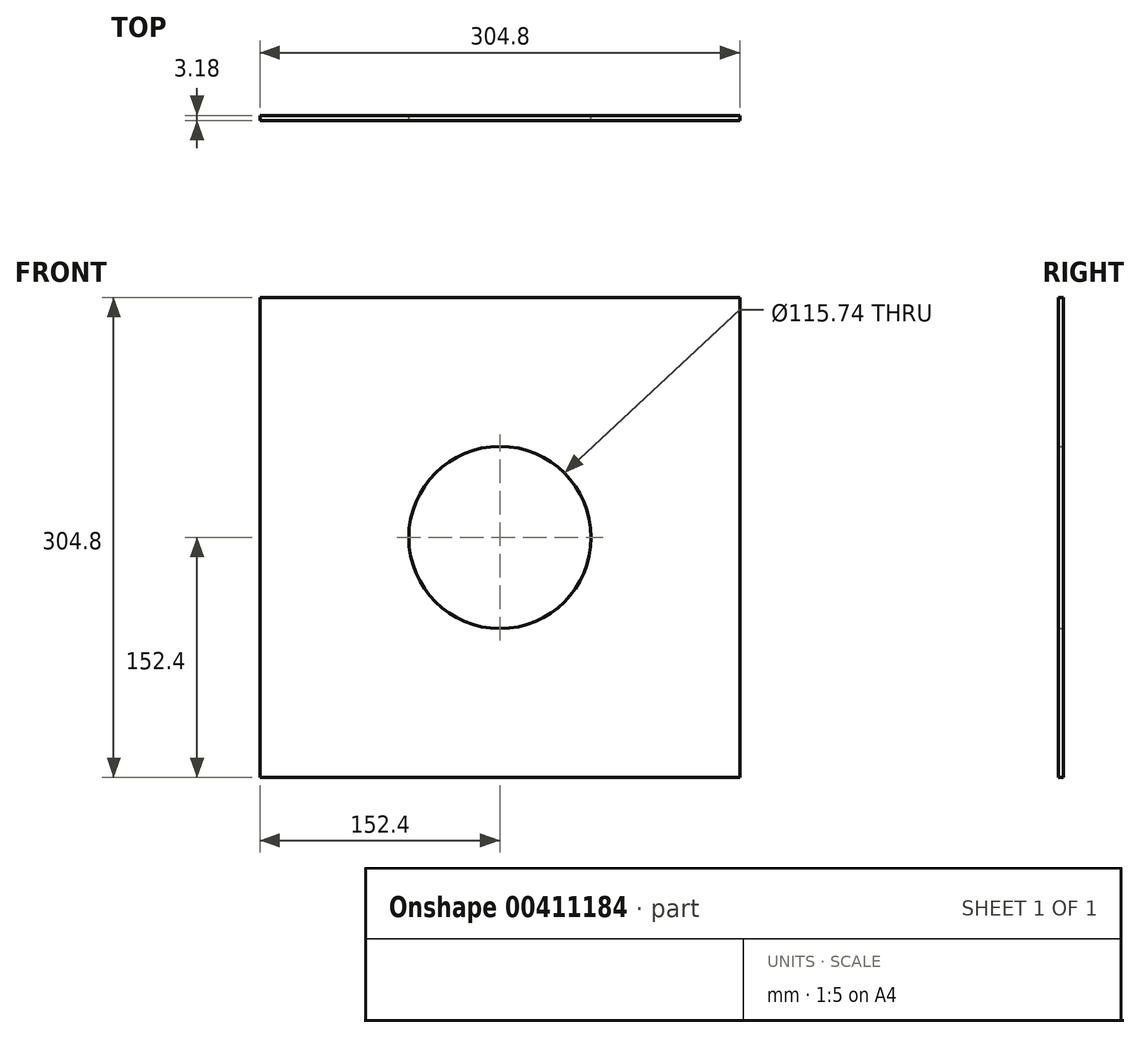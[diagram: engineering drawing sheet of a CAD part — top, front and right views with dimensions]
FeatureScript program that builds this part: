
annotation { "Feature Type Name" : "Feature", "Feature Type Description" : "" }
export const myFeature = defineFeature(function(context is Context, id is Id, definition is map)
    precondition{}
    {
        {
            var Q0;
            Q0=qCreatedBy(makeId("Front.planeOp"),FACE);
            var sketch = newSketch(context, id + "F0", { "sketchPlane" : qUnion([Q0])});
            skLineSegment(sketch, "E0.bottom", {"start": v(-152.4, 152.4) * mm, "end": v(152.4, 152.4) * mm});
            skLineSegment(sketch, "E0.top", {"start": v(-152.4, -152.4) * mm, "end": v(152.4, -152.4) * mm});
            skLineSegment(sketch, "E0.left", {"start": v(-152.4, 152.4) * mm, "end": v(-152.4, -152.4) * mm});
            skLineSegment(sketch, "E0.right", {"start": v(152.4, 152.4) * mm, "end": v(152.4, -152.4) * mm});
            skPoint(sketch, "E0.middle", {"position": v(0, 0) * mm});
            skCircle(sketch, "E1", {"center": v(0, 0) * mm, "radius": 57.87 * mm});
            skSolve(sketch);
        }
        {
            var Q0;
            Q0=makeQuery(id+"F0.imprint","IMPRINT",FACE,{"disambiguationData":[TD([[makeQuery(id+"F0.imprint","IMPRINT",EDGE,{"derivedFrom":sQuery(id+"F0.wireOp",EDGE,"E0.bottom")}),-1.0]])]});
            extrude(context, id + "F1", {"entities" : qUnion([Q0]), "depth" : 3.17 * mm});
        }
    });
